# Revit family: LAMP_HANCE TRACK MEDIUM FLOOD (DALI)
name_source: partatom
category: Modelos genéricos
revit_build: Autodesk Revit 2015 (Build: 20140606_1530(x64)
units: mm (PartAtom-declared; Revit-internal decimal feet)

## types (16) — shared parameters
CRI = 80
Comentarios de tipo = Availability of tilting between 0º and 90º, rotation between 0º and 355º and change ring color when placed in a project.
Elevación por defecto = 1219 mm
Fabricante = LAMP
Gear = Adjustable DALI
Installation instructions = http://www.lamp.es
Insulation class = I
Lamp = LED COB
Last update = 08/08/2018
Luminaire type = Indoor - Spotlight
MacAdam = 3
Manufacturer URL = http://www.lamp.es
Manufacturer country = Spain
Manufacturer name = LAMP
Model explanation = Availability of tilting between 0º and 90º, rotation between 0º and 355º and change ring color when placed in a project.
Power Supply = 220-240V 50-60Hz
Product URL = http://www.lamp.es
Product datasheet = http://www.lamp.es
Protection rating = IP20
Type = COB PHILIPS

## per-type parameters (varying)
| type | Altura tija | Anchura tija | Body height | Descripción | Diameter | Efficacy | Finish | IEE | Initial color | Initial intensity | LED Lifetime | Longitud aro | Longitud cuerpo | Material tija | Material track | Modelo | Photometric web file | Plum | Power | Product code | Profundidad tija | Total height | Weight |
| 751LM 3000 BLACK | 63 mm  [stored 0.206693 ft] | 23 mm  [stored 0.0754593 ft] | 135 mm  [stored 0.442913 ft] | HANCE TRACK 220 1000 WW MFL BK. | 65 mm  [stored 0.213255 ft] | 92 lm/W | Texturised black | A+ | 3000 K | 751 lm | 50.000 L90 B10 | 64 mm | 135 mm  [stored 0.442913 ft] | LAMP_Aluminio Hance Negro | LAMP_Aluminio Hance Negro | HS1TK10MF830DBB | Cuerpo Hance TRACK MEDIUM FLOOD (tilting) : 751LM 3000 BLACK | 8 W | 7 W | HS1TK10MF830DBB | 8 mm  [stored 0.0262467 ft] | 190 mm | 0.47 kg |
| 751LM 3000 WHITE | 63 mm  [stored 0.206693 ft] | 23 mm  [stored 0.0754593 ft] | 135 mm  [stored 0.442913 ft] | HANCE TRACK 220 1000 WW MFL WH. | 65 mm  [stored 0.213255 ft] | 92 lm/W | Texturised matt white | A+ | 3000 K | 751 lm | 50.000 L90 B10 | 64 mm | 135 mm  [stored 0.442913 ft] | LAMP_Aluminio Hance Blanco | LAMP_Aluminio Hance Blanco | HS1TK10MF830DBW | Cuerpo Hance TRACK MEDIUM FLOOD (tilting) : 751LM 3000 WHITE | 8 W | 7 W | HS1TK10MF830DBW | 8 mm  [stored 0.0262467 ft] | 190 mm | 0.47 kg |
| 794LM 4000 BLACK | 63 mm  [stored 0.206693 ft] | 23 mm  [stored 0.0754593 ft] | 135 mm  [stored 0.442913 ft] | HANCE TRACK 220 1000 NW MFL BK. | 65 mm  [stored 0.213255 ft] | 97 lm/W | Texturised black | A++ | 4000 K | 794 lm | 50.000 L90 B10 | 64 mm | 135 mm  [stored 0.442913 ft] | LAMP_Aluminio Hance Negro | LAMP_Aluminio Hance Negro | HS1TK10MF840DBB | Cuerpo Hance TRACK MEDIUM FLOOD (tilting) : 794LM 4000 BLACK | 8 W | 7 W | HS1TK10MF840DBB | 8 mm  [stored 0.0262467 ft] | 190 mm | 0.47 kg |
| 794LM 4000 WHITE | 63 mm  [stored 0.206693 ft] | 23 mm  [stored 0.0754593 ft] | 135 mm  [stored 0.442913 ft] | HANCE TRACK 220 1000 NW MFL WH. | 65 mm  [stored 0.213255 ft] | 97 lm/W | Texturised matt white | A++ | 4000 K | 794 lm | 50.000 L90 B10 | 64 mm | 135 mm  [stored 0.442913 ft] | LAMP_Aluminio Hance Blanco | LAMP_Aluminio Hance Blanco | HS1TK10MF840DBW | Cuerpo Hance TRACK MEDIUM FLOOD (tilting) : 794LM 4000 WHITE | 8 W | 7 W | HS1TK10MF840DBW | 8 mm  [stored 0.0262467 ft] | 190 mm | 0.47 kg |
| 1612LM 3000 BLACK | 63 mm  [stored 0.206693 ft] | 23 mm  [stored 0.0754593 ft] | 170 mm  [stored 0.557743 ft] | HANCE TRACK 220 2000 WW MFL BK. | 65 mm  [stored 0.213255 ft] | 77 lm/W | Texturised black | A+ | 3000 K | 1612 lm | 50.000 L80 B10 | 99 mm | 170 mm  [stored 0.557743 ft] | LAMP_Aluminio Hance Negro | LAMP_Aluminio Hance Negro | HS1TK20MF830DBB | Cuerpo Hance TRACK MEDIUM FLOOD (tilting) : 1612LM 3000 BLACK | 21 W | 18 W | HS1TK20MF830DBB | 8 mm  [stored 0.0262467 ft] | 225 mm  [stored 0.738189 ft] | 0.65 kg |
| 1612LM 3000 WHITE | 63 mm  [stored 0.206693 ft] | 23 mm  [stored 0.0754593 ft] | 170 mm  [stored 0.557743 ft] | HANCE TRACK 220 2000 WW MFL WH. | 65 mm  [stored 0.213255 ft] | 77 lm/W | Texturised matt white | A+ | 3000 K | 1612 lm | 50.000 L80 B10 | 99 mm | 170 mm  [stored 0.557743 ft] | LAMP_Aluminio Hance Blanco | LAMP_Aluminio Hance Blanco | HS1TK20MF830DBW | Cuerpo Hance TRACK MEDIUM FLOOD (tilting) : 1612LM 3000 WHITE | 21 W | 18 W | HS1TK20MF830DBW | 8 mm  [stored 0.0262467 ft] | 225 mm  [stored 0.738189 ft] | 0.65 kg |
| 1703LM 4000 BLACK | 63 mm  [stored 0.206693 ft] | 23 mm  [stored 0.0754593 ft] | 170 mm  [stored 0.557743 ft] | HANCE TRACK 220 2000 NW MFL BK. | 65 mm  [stored 0.213255 ft] | 81 lm/W | Texturised black | A+ | 4000 K | 1703 lm | 50.000 L80 B10 | 99 mm | 170 mm  [stored 0.557743 ft] | LAMP_Aluminio Hance Negro | LAMP_Aluminio Hance Negro | HS1TK20MF840DBB | Cuerpo Hance TRACK MEDIUM FLOOD (tilting) : 1703LM 4000 BLACK | 21 W | 18 W | HS1TK20MF840DBB | 8 mm  [stored 0.0262467 ft] | 225 mm  [stored 0.738189 ft] | 0.65 kg |
| 1703LM 4000 WHITE | 63 mm  [stored 0.206693 ft] | 23 mm  [stored 0.0754593 ft] | 170 mm  [stored 0.557743 ft] | HANCE TRACK 220 2000 NW MFL WH. | 65 mm  [stored 0.213255 ft] | 81 lm/W | Texturised matt white | A+ | 4000 K | 1703 lm | 50.000 L80 B10 | 99 mm | 170 mm  [stored 0.557743 ft] | LAMP_Aluminio Hance Blanco | LAMP_Aluminio Hance Blanco | HS1TK20MF840DBW | Cuerpo Hance TRACK MEDIUM FLOOD (tilting) : 1703LM 4000 WHITE | 21 W | 18 W | HS1TK20MF840DBW | 8 mm  [stored 0.0262467 ft] | 225 mm  [stored 0.738189 ft] | 0.65 kg |
| 2625LM 3000 BLACK | 49 mm  [stored 0.160761 ft] | 28 mm  [stored 0.0918635 ft] | 210 mm  [stored 0.688976 ft] | HANCE TRACK 220 3000 WW MFL BK. | 90 mm  [stored 0.295276 ft] | 92 lm/W | Texturised black | A+ | 3000 K | 2625 lm | 50.000 L80 B10 | 139 mm | 210 mm  [stored 0.688976 ft] | LAMP_Aluminio Hance Negro | LAMP_Aluminio Hance Negro | HS1TK30MF830DBB | Cuerpo Hance TRACK MEDIUM FLOOD (tilting) : 2625LM 3000 BLACK | 29 W | 26 W | HS1TK30MF830DBB | 18 mm  [stored 0.0590551 ft] | 265 mm  [stored 0.869423 ft] | 1.35 kg |
| 2625LM 3000 WHITE | 49 mm  [stored 0.160761 ft] | 28 mm  [stored 0.0918635 ft] | 210 mm  [stored 0.688976 ft] | HANCE TRACK 220 3000 WW MFL WH. | 90 mm  [stored 0.295276 ft] | 92 lm/W | Texturised matt white | A+ | 3000 K | 2625 lm | 50.000 L80 B10 | 139 mm | 210 mm  [stored 0.688976 ft] | LAMP_Aluminio Hance Blanco | LAMP_Aluminio Hance Blanco | HS1TK30MF830DBW | Cuerpo Hance TRACK MEDIUM FLOOD (tilting) : 2625LM 3000 WHITE | 29 W | 26 W | HS1TK30MF830DBW | 18 mm  [stored 0.0590551 ft] | 265 mm  [stored 0.869423 ft] | 1.35 kg |
| 2744LM 4000 BLACK | 49 mm  [stored 0.160761 ft] | 28 mm  [stored 0.0918635 ft] | 210 mm  [stored 0.688976 ft] | HANCE TRACK 220 3000 NW MFL BK. | 90 mm  [stored 0.295276 ft] | 96 lm/W | Texturised black | A+ | 4000 K | 2744 lm | 50.000 L80 B10 | 139 mm | 210 mm  [stored 0.688976 ft] | LAMP_Aluminio Hance Negro | LAMP_Aluminio Hance Negro | HS1TK30MF840DBB | Cuerpo Hance TRACK MEDIUM FLOOD (tilting) : 2744LM 4000 BLACK | 29 W | 26 W | HS1TK30MF840DBB | 18 mm  [stored 0.0590551 ft] | 265 mm  [stored 0.869423 ft] | 1.35 kg |
| 2744LM 4000 WHITE | 49 mm  [stored 0.160761 ft] | 28 mm  [stored 0.0918635 ft] | 210 mm  [stored 0.688976 ft] | HANCE TRACK 220 3000 NW MFL WH. | 90 mm  [stored 0.295276 ft] | 96 lm/W | Texturised matt white | A+ | 4000 K | 2744 lm | 50.000 L80 B10 | 139 mm | 210 mm  [stored 0.688976 ft] | LAMP_Aluminio Hance Blanco | LAMP_Aluminio Hance Blanco | HS1TK30MF840DBW | Cuerpo Hance TRACK MEDIUM FLOOD (tilting) : 2744LM 4000 WHITE | 29 W | 26 W | HS1TK30MF840DBW | 18 mm  [stored 0.0590551 ft] | 265 mm  [stored 0.869423 ft] | 1.35 kg |
| 3387LM 3000 BLACK | 49 mm  [stored 0.160761 ft] | 28 mm  [stored 0.0918635 ft] | 210 mm  [stored 0.688976 ft] | HANCE TRACK 220 4000 WW MFL BK. | 90 mm  [stored 0.295276 ft] | 86 lm/W | Texturised black | A+ | 3000 K | 3387 lm | 50.000 L80 B10 | 139 mm | 210 mm  [stored 0.688976 ft] | LAMP_Aluminio Hance Negro | LAMP_Aluminio Hance Negro | HS1TK40MF830DBB | Cuerpo Hance TRACK MEDIUM FLOOD (tilting) : 3387LM 3000 BLACK | 40 W | 35 W | HS1TK40MF830DBB | 18 mm  [stored 0.0590551 ft] | 265 mm  [stored 0.869423 ft] | 1.35 kg |
| 3387LM 3000 WHITE | 49 mm  [stored 0.160761 ft] | 28 mm  [stored 0.0918635 ft] | 210 mm  [stored 0.688976 ft] | HANCE TRACK 220 4000 WW MFL WH. | 90 mm  [stored 0.295276 ft] | 86 lm/W | Texturised matt white | A+ | 3000 K | 3387 lm | 50.000 L80 B10 | 139 mm | 210 mm  [stored 0.688976 ft] | LAMP_Aluminio Hance Blanco | LAMP_Aluminio Hance Blanco | HS1TK40MF830DBW | Cuerpo Hance TRACK MEDIUM FLOOD (tilting) : 3387LM 3000 WHITE | 40 W | 35 W | HS1TK40MF830DBW | 18 mm  [stored 0.0590551 ft] | 265 mm  [stored 0.869423 ft] | 1.35 kg |
| 3527LM 4000 BLACK | 49 mm  [stored 0.160761 ft] | 28 mm  [stored 0.0918635 ft] | 210 mm  [stored 0.688976 ft] | HANCE TRACK 220 4000 NW MFL BK. | 90 mm  [stored 0.295276 ft] | 89 lm/W | Texturised black | A+ | 4000 K | 3527 lm | 50.000 L80 B10 | 139 mm | 210 mm  [stored 0.688976 ft] | LAMP_Aluminio Hance Negro | LAMP_Aluminio Hance Negro | HS1TK40MF840DBB | Cuerpo Hance TRACK MEDIUM FLOOD (tilting) : 3527LM 4000 BLACK | 40 W | 35 W | HS1TK40MF840DBB | 18 mm  [stored 0.0590551 ft] | 265 mm  [stored 0.869423 ft] | 1.35 kg |
| 3527LM 4000 WHITE | 49 mm  [stored 0.160761 ft] | 28 mm  [stored 0.0918635 ft] | 210 mm  [stored 0.688976 ft] | HANCE TRACK 220 4000 NW MFL WH. | 90 mm  [stored 0.295276 ft] | 89 lm/W | Texturised matt white | A+ | 4000 K | 3527 lm | 50.000 L80 B10 | 139 mm | 210 mm  [stored 0.688976 ft] | LAMP_Aluminio Hance Blanco | LAMP_Aluminio Hance Blanco | HS1TK40MF840DBW | Cuerpo Hance TRACK MEDIUM FLOOD (tilting) : 3527LM 4000 WHITE | 40 W | 35 W | HS1TK40MF840DBW | 18 mm  [stored 0.0590551 ft] | 265 mm  [stored 0.869423 ft] | 1.35 kg |

note: [stored X ft] marks values corroborated as IEEE doubles in the binary element streams (Revit-internal decimal feet)
